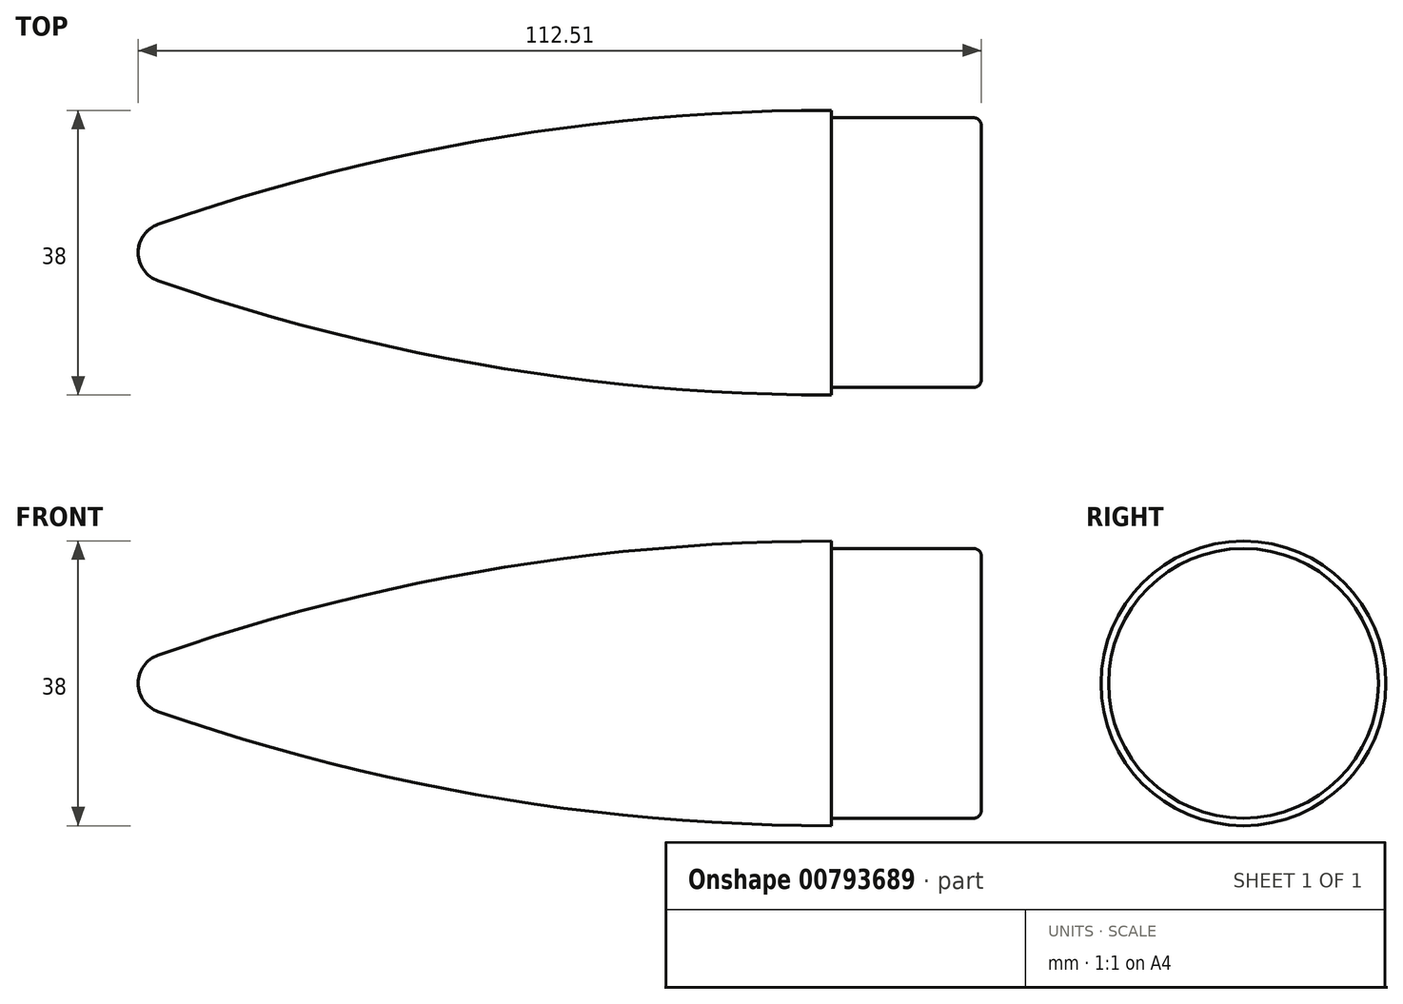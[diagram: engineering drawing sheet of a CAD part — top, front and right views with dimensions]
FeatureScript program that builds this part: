
annotation { "Feature Type Name" : "Feature", "Feature Type Description" : "" }
export const myFeature = defineFeature(function(context is Context, id is Id, definition is map)
    precondition{}
    {
        {
            var Q0;
            Q0=qCreatedBy(makeId("Top.planeOp"),FACE);
            var sketch = newSketch(context, id + "F0", { "sketchPlane" : qUnion([Q0])});
            skLineSegment(sketch, "E0", {"start": v(100, 0) * mm, "end": v(-49.92, 0) * mm, "construction": true});
            skLineSegment(sketch, "E1", {"start": v(100, 0) * mm, "end": v(100, 19) * mm, "construction": true});
            skLineSegment(sketch, "E2", {"start": v(-37.94, 19) * mm, "end": v(100, 19) * mm, "construction": true});
            skLineSegment(sketch, "E3.bottom", {"start": v(100, 18) * mm, "end": v(119, 18) * mm});
            skLineSegment(sketch, "E3.right", {"start": v(120, 17) * mm, "end": v(120, 0) * mm});
            skLineSegment(sketch, "E4", {"start": v(100, 19) * mm, "end": v(100, 18) * mm});
            skLineSegment(sketch, "E5", {"start": v(0, 0) * mm, "end": v(120, 0) * mm});
            skLineSegment(sketch, "E6.left", {"start": v(100, 19) * mm, "end": v(100, 19) * mm});
            skLineSegment(sketch, "E7.bottom", {"start": v(0, 0) * mm, "end": v(115, 0) * mm});
            skPoint(sketch, "E8.visualSharp", {"position": v(120, 18) * mm});
            skArc(sketch, "E8.filletArc", {"start": v(120, 17) * mm, "mid": v(119.7, 17.7) * mm, "end": v(119, 18) * mm});
            skSolve(sketch);
        }
        {
            var Q0;
            Q0=qCreatedBy(makeId("Top.planeOp"),FACE);
            var sketch = newSketch(context, id + "F1", { "sketchPlane" : qUnion([Q0])});
            skCircle(sketch, "E9.0", {"center": v(100, -253.66) * mm, "radius": 272.66 * mm});
            skCircle(sketch, "E10", {"center": v(11.49, 0) * mm, "radius": 4 * mm});
            skLineSegment(sketch, "E11.0", {"start": v(0, 0) * mm, "end": v(120, 0) * mm});
            skLineSegment(sketch, "E12.0", {"start": v(120, 17) * mm, "end": v(120, 0) * mm});
            skArc(sketch, "E12.1", {"start": v(120, 17) * mm, "mid": v(119.7, 17.7) * mm, "end": v(119, 18) * mm});
            skLineSegment(sketch, "E12.2", {"start": v(100, 18) * mm, "end": v(119, 18) * mm});
            skLineSegment(sketch, "E13.0", {"start": v(100, 19) * mm, "end": v(100, 18) * mm});
            skLineSegment(sketch, "E14.0", {"start": v(-37.94, 19) * mm, "end": v(100, 19) * mm, "construction": true});
            skSolve(sketch);
        }
        {
            var Q0;
            {var subQ0=sQuery(id+"F1.wireOp",EDGE,"E12.0");Q0=makeQuery(id+"F1.imprint","IMPRINT",FACE,{"disambiguationData":[TD([[makeQuery(id+"F1.imprint","IMPRINT",EDGE,{"derivedFrom":subQ0}),-1.0]])]});}
            var Q1;
            {var subQ0=sQuery(id+"F1.wireOp",EDGE,"E10");var subQ1=makeQuery(id+"F1.imprint","INTERSECT",VERTEX,{"derivedFrom":[sQuery(id+"F1.wireOp",EDGE,"E9.0"),subQ0]});Q1=makeQuery(id+"F1.imprint","IMPRINT",FACE,{"disambiguationData":[TD([[makeQuery(id+"F1.imprint","IMPRINT",EDGE,{"disambiguationData":[TD([[subQ1,1.0]])],"derivedFrom":subQ0}),1.0]])]});}
            var Q2;
            Q2=sQuery(id+"F0.wireOp",EDGE,"E5");
            revolve(context, id + "F2", {"surfaceOperationType" : NewSurfaceOperationType.NEW, "entities" : qUnion([Q0, Q1]), "axis" : qUnion([Q2]), "revolveType" : RevolveType.FULL});
        }
    });
